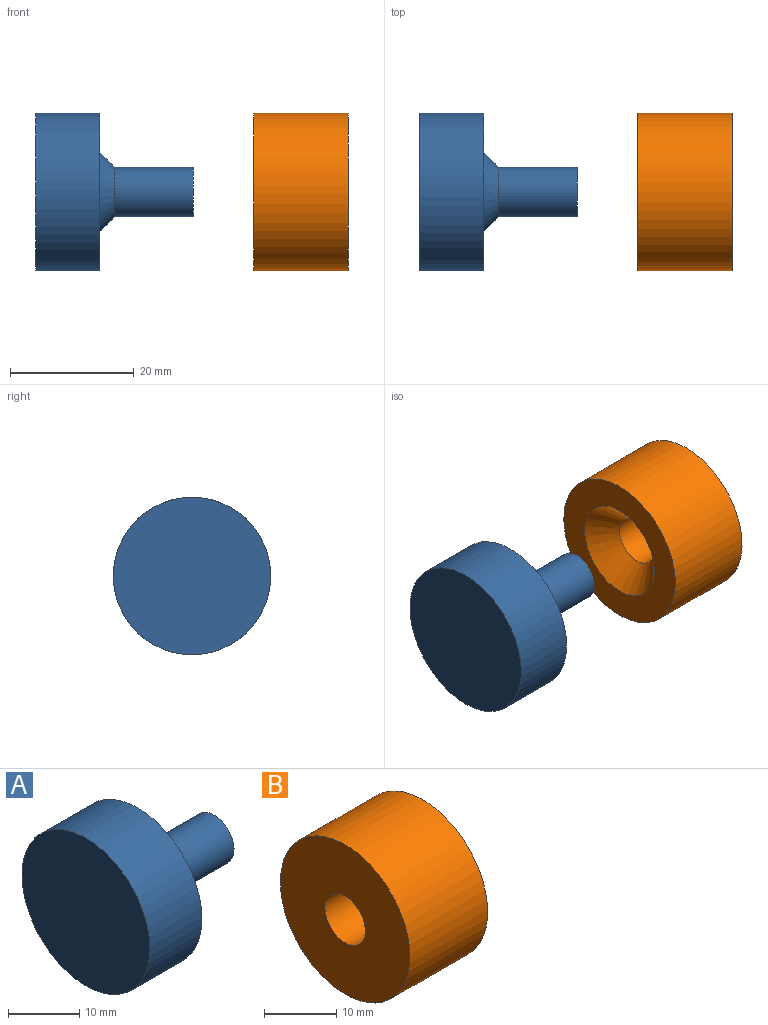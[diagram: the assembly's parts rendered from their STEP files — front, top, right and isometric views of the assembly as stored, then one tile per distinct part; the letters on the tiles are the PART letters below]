
ASSEMBLY  parts=2 mates=1
PART A: 6 faces, bbox 25.4x25.4x25.4 mm
  f0: plane 7.95x7.95mm, normal (1,0,0), area 49.6mm2, adj f1
  f1: cylinder r=3.98mm len=12.7mm, axis (1,0,0), area 317.2mm2, adj f0,f2
  f2: cone r=6.35mm half-angle=45deg, axis (-1,0,0), area 108.9mm2, adj f1,f3
  f3: plane 25.4x25.4mm, normal (1,0,0), area 380mm2, adj f2,f4
  f4: cylinder r=12.7mm len=25.4mm, axis (1,0,0), area 823.9mm2, adj f3,f5
  f5: plane 25.4x25.4mm, normal (-1,0,0), area 506.7mm2, adj f4
PART B: 5 faces, bbox 15.2x25.4x25.4 mm
  f0: plane 25.4x25.4mm, normal (-1,0,0), area 457.1mm2, adj f1,f4
  f1: cylinder r=3.98mm len=11.28mm, axis (1,0,0), area 281.7mm2, adj f0,f2
  f2: cone r=3.98mm half-angle=45deg, axis (1,0,0), area 209.7mm2, adj f1,f3
  f3: plane 25.4x25.4mm, normal (1,0,0), area 308.8mm2, adj f2,f4
  f4: cylinder r=12.7mm len=25.4mm, axis (1,0,0), area 1216.1mm2, adj f0,f3
PLACE A t=(0.03,-0.28,-0.38)mm fixed
PLACE B rot(axis=(0,1,0),180deg) t=(9.73,-0.28,-0.38)mm
MATE slider B.f1 <-> A.f1  axis (1,0,0) through (24.97,-0.28,-0.38)mm
